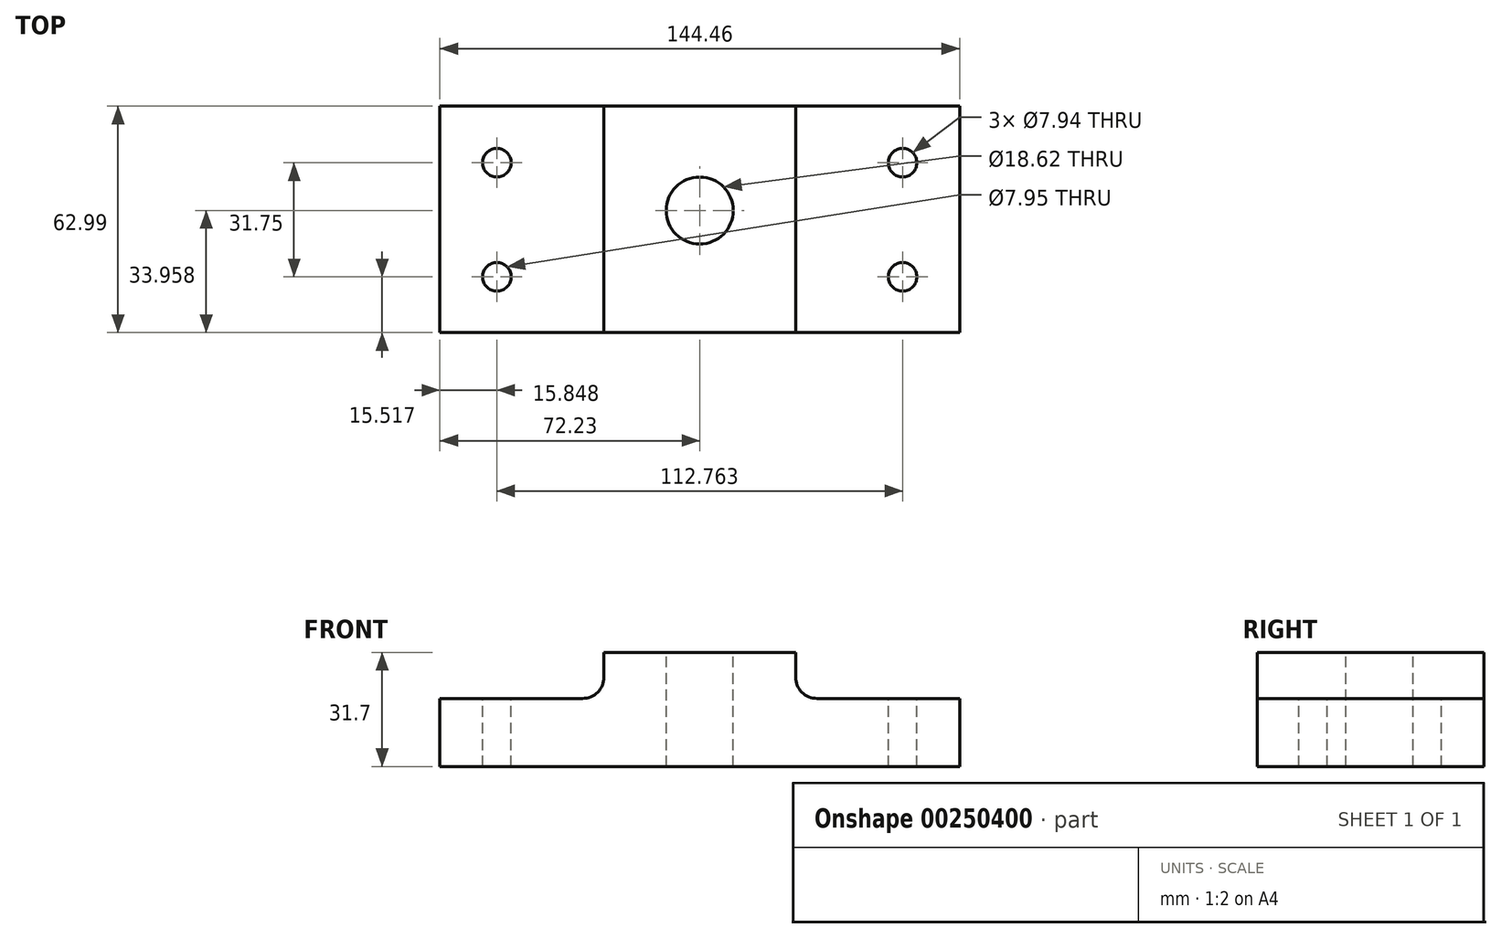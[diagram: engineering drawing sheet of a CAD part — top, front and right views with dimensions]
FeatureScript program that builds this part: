
annotation { "Feature Type Name" : "Feature", "Feature Type Description" : "" }
export const myFeature = defineFeature(function(context is Context, id is Id, definition is map)
    precondition{}
    {
        {
            var Q0;
            Q0=qCreatedBy(makeId("Front.planeOp"),FACE);
            var sketch = newSketch(context, id + "F0", { "sketchPlane" : qUnion([Q0])});
            skLineSegment(sketch, "E0.bottom", {"start": v(72.23, -15.85) * mm, "end": v(-72.23, -15.85) * mm});
            skLineSegment(sketch, "E0.top", {"start": v(72.23, 15.85) * mm, "end": v(-72.23, 15.85) * mm});
            skLineSegment(sketch, "E0.left", {"start": v(72.23, -15.85) * mm, "end": v(72.23, 15.85) * mm});
            skLineSegment(sketch, "E0.right", {"start": v(-72.23, -15.85) * mm, "end": v(-72.23, 15.85) * mm});
            skPoint(sketch, "E0.middle", {"position": v(0, 0) * mm});
            skSolve(sketch);
        }
        {
            var Q0;
            Q0=makeQuery(id+"F0.imprint","IMPRINT",FACE,{"disambiguationData":[TD([[makeQuery(id+"F0.imprint","IMPRINT",EDGE,{"derivedFrom":sQuery(id+"F0.wireOp",EDGE,"E0.bottom")}),-1.0]])]});
            extrude(context, id + "F1", {"entities" : qUnion([Q0]), "depth" : 63 * mm});
        }
        {
            var Q0;
            Q0=makeQuery(id+"F1.opExtrude","CAP_FACE",FACE,{"disambiguationData":[OSD([sQuery(id+"F0.wireOp",EDGE,"E0.bottom"),sQuery(id+"F0.wireOp",EDGE,"E0.top"),sQuery(id+"F0.wireOp",EDGE,"E0.left"),sQuery(id+"F0.wireOp",EDGE,"E0.right")])],"isStart":false});
            var sketch = newSketch(context, id + "F2", { "sketchPlane" : qUnion([Q0])});
            skLineSegment(sketch, "E1", {"start": v(-72.23, -15.85) * mm, "end": v(-72.23, 3.07) * mm});
            skLineSegment(sketch, "E2", {"start": v(-72.23, 3.07) * mm, "end": v(-26.63, 3.07) * mm});
            skLineSegment(sketch, "E3", {"start": v(72.23, -15.85) * mm, "end": v(72.23, 3.07) * mm});
            skLineSegment(sketch, "E4", {"start": v(72.23, 3.07) * mm, "end": v(26.63, 3.07) * mm});
            skLineSegment(sketch, "E5", {"start": v(-26.63, 3.07) * mm, "end": v(-26.63, 15.85) * mm});
            skLineSegment(sketch, "E6", {"start": v(26.63, 3.07) * mm, "end": v(26.63, 15.85) * mm});
            skLineSegment(sketch, "E7", {"start": v(26.63, 15.85) * mm, "end": v(-26.63, 15.85) * mm});
            skSolve(sketch);
        }
        {
            var Q0;
            {var subQ0=sQuery(id+"F2.wireOp",EDGE,"E2");Q0=makeQuery(id+"F2.imprint","IMPRINT",FACE,{"disambiguationData":[TD([[makeQuery(id+"F2.imprint","IMPRINT",EDGE,{"derivedFrom":subQ0}),1.0]])]});}
            var Q1;
            {var subQ0=sQuery(id+"F2.wireOp",EDGE,"E4");Q1=makeQuery(id+"F2.imprint","IMPRINT",FACE,{"disambiguationData":[TD([[makeQuery(id+"F2.imprint","IMPRINT",EDGE,{"derivedFrom":subQ0}),-1.0]])]});}
            extrude(context, id + "F3", {"entities" : qUnion([Q0, Q1]), "operationType" : NewBodyOperationType.REMOVE, "endBound" : BoundingType.THROUGH_ALL, "oppositeDirection" : true, "depth" : 25.4 * mm});
        }
        {
            var Q0;
            Q0=makeQuery(id+"F3.boolean.opBoolean","COPY",EDGE,{"derivedFrom":makeQuery(id+"F3.opExtrude","SWEPT_EDGE",EDGE,{"disambiguationData":[OSD([sQuery(id+"F2.wireOp",EDGE,"E2"),sQuery(id+"F2.wireOp",EDGE,"E5")])]})});
            var Q1;
            Q1=makeQuery(id+"F3.boolean.opBoolean","COPY",EDGE,{"derivedFrom":makeQuery(id+"F3.opExtrude","SWEPT_EDGE",EDGE,{"disambiguationData":[OSD([sQuery(id+"F2.wireOp",EDGE,"E4"),sQuery(id+"F2.wireOp",EDGE,"E6")])]})});
            fillet(context, id + "F4", {"entities" : qUnion([Q0, Q1]), "radius" : 5.95 * mm, "tangentPropagation" : true, "allowEdgeOverflow" : false});
        }
        {
            var Q0;
            Q0=makeQuery(id+"F1.opExtrude","SWEPT_FACE",FACE,{"disambiguationData":[OSD([sQuery(id+"F0.wireOp",EDGE,"E0.top")])]});
            var sketch = newSketch(context, id + "F5", { "sketchPlane" : qUnion([Q0])});
            skCircle(sketch, "E8", {"center": v(0, -29.03) * mm, "radius": 9.3 * mm});
            skSolve(sketch);
        }
        {
            var Q0;
            Q0=makeQuery(id+"F5.imprint","IMPRINT",FACE,{"disambiguationData":[TD([[makeQuery(id+"F5.imprint","IMPRINT",EDGE,{"derivedFrom":sQuery(id+"F5.wireOp",EDGE,"E8")}),1.0]])]});
            extrude(context, id + "F6", {"entities" : qUnion([Q0]), "operationType" : NewBodyOperationType.REMOVE, "endBound" : BoundingType.THROUGH_ALL, "oppositeDirection" : true, "depth" : 25.4 * mm});
        }
        {
            var Q0;
            Q0=makeQuery(id+"F3.boolean.opBoolean","COPY",FACE,{"derivedFrom":makeQuery(id+"F3.opExtrude","SWEPT_FACE",FACE,{"disambiguationData":[OSD([sQuery(id+"F2.wireOp",EDGE,"E2")])]})});
            var sketch = newSketch(context, id + "F7", { "sketchPlane" : qUnion([Q0])});
            skCircle(sketch, "E9", {"center": v(-56.38, -15.72) * mm, "radius": 3.97 * mm});
            skCircle(sketch, "E10", {"center": v(-56.38, -47.47) * mm, "radius": 3.98 * mm});
            skSolve(sketch);
        }
        {
            var Q0;
            Q0=makeQuery(id+"F7.imprint","IMPRINT",FACE,{"disambiguationData":[TD([[makeQuery(id+"F7.imprint","IMPRINT",EDGE,{"derivedFrom":sQuery(id+"F7.wireOp",EDGE,"E9")}),1.0]])]});
            var Q1;
            Q1=makeQuery(id+"F7.imprint","IMPRINT",FACE,{"disambiguationData":[TD([[makeQuery(id+"F7.imprint","IMPRINT",EDGE,{"derivedFrom":sQuery(id+"F7.wireOp",EDGE,"E10")}),1.0]])]});
            extrude(context, id + "F8", {"entities" : qUnion([Q0, Q1]), "operationType" : NewBodyOperationType.REMOVE, "endBound" : BoundingType.THROUGH_ALL, "oppositeDirection" : true, "depth" : 25.4 * mm});
        }
        {
            var Q0;
            Q0=makeQuery(id+"F3.boolean.opBoolean","COPY",FACE,{"derivedFrom":makeQuery(id+"F3.opExtrude","SWEPT_FACE",FACE,{"disambiguationData":[OSD([sQuery(id+"F2.wireOp",EDGE,"E4")])]})});
            var sketch = newSketch(context, id + "F9", { "sketchPlane" : qUnion([Q0])});
            skCircle(sketch, "E11", {"center": v(56.38, -15.72) * mm, "radius": 3.97 * mm});
            skCircle(sketch, "E12", {"center": v(56.38, -47.47) * mm, "radius": 3.97 * mm});
            skSolve(sketch);
        }
        {
            var Q0;
            Q0=makeQuery(id+"F9.imprint","IMPRINT",FACE,{"disambiguationData":[TD([[makeQuery(id+"F9.imprint","IMPRINT",EDGE,{"derivedFrom":sQuery(id+"F9.wireOp",EDGE,"E11")}),1.0]])]});
            var Q1;
            Q1=makeQuery(id+"F9.imprint","IMPRINT",FACE,{"disambiguationData":[TD([[makeQuery(id+"F9.imprint","IMPRINT",EDGE,{"derivedFrom":sQuery(id+"F9.wireOp",EDGE,"E12")}),1.0]])]});
            extrude(context, id + "F10", {"entities" : qUnion([Q0, Q1]), "operationType" : NewBodyOperationType.REMOVE, "endBound" : BoundingType.THROUGH_ALL, "oppositeDirection" : true, "depth" : 25.4 * mm});
        }
    });
